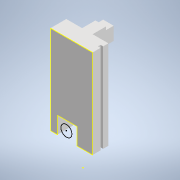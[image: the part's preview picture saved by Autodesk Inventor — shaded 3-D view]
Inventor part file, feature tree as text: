
AUTODESK INVENTOR PART (.ipt)
format: ipt  version: 2020 (Build 240168000, 168)  size: 191,488 bytes
history: native  units: mm
features: reference x17, extrude x9, sketch x9, other x8, projected_geometry x6
ambient origin geometry x8: Origin, YZ Plane, XZ Plane, XY Plane, X Axis, Y Axis, Z Axis, Center Point
bodies: Body1 (feature_tree)
feature tree (49):
  other  "솔리드1"
  extrude  "돌출1"  Depth=20.0mm TaperAngle=0.0deg
  extrude  "돌출2"  Depth=25.3mm TaperAngle=0.0deg
  extrude  "돌출3"  Depth=137.5mm
  extrude  "돌출4"  Depth=40.0mm TaperAngle=0.0deg
  extrude  "돌출5"  Depth=30.0mm TaperAngle=0.0deg
  extrude  "돌출6"  Depth=10.0mm
  extrude  "돌출7"  Depth=15.0mm
  extrude  "돌출8"  Depth=5.0mm TaperAngle=0.0deg
  extrude  "돌출9"  Depth=32.0mm
  sketch  "스케치1"
  reference  "참조1"
  reference  "참조2"
  reference  "참조3"
  reference  "참조4"
  reference  "참조5"
  reference  "참조6"
  reference  "참조7"
  reference  "참조8"
  sketch  "스케치2"
  reference  "참조9"
  reference  "참조10"
  reference  "참조11"
  sketch  "스케치3"
  reference  "참조12"
  reference  "참조13"
  sketch  "스케치4"
  reference  "참조14"
  reference  "참조15"
  reference  "참조16"
  reference  "참조17"
  sketch  "스케치6"
  projected_geometry  "투영된 루프1"
  sketch  "스케치7"
  projected_geometry  "투영된 루프2"
  projected_geometry  "투영된 루프3"
  sketch  "스케치8"
  projected_geometry  "투영된 루프4"
  sketch  "스케치9"
  projected_geometry  "투영된 루프5"
  sketch  "스케치10"
  projected_geometry  "투영된 루프6"
  other  "<userpath>\Documents\Inventor\CoMoVi\Package\v6.iam"
  other  "v6.iam"
  other  "AL_profile_final:1"
  other  "AL_profile_final:2"
  other  "cross_AL_profile:2"
  other  "caster_wheel_mount:1"
  other  "cross_AL_profile:1"
